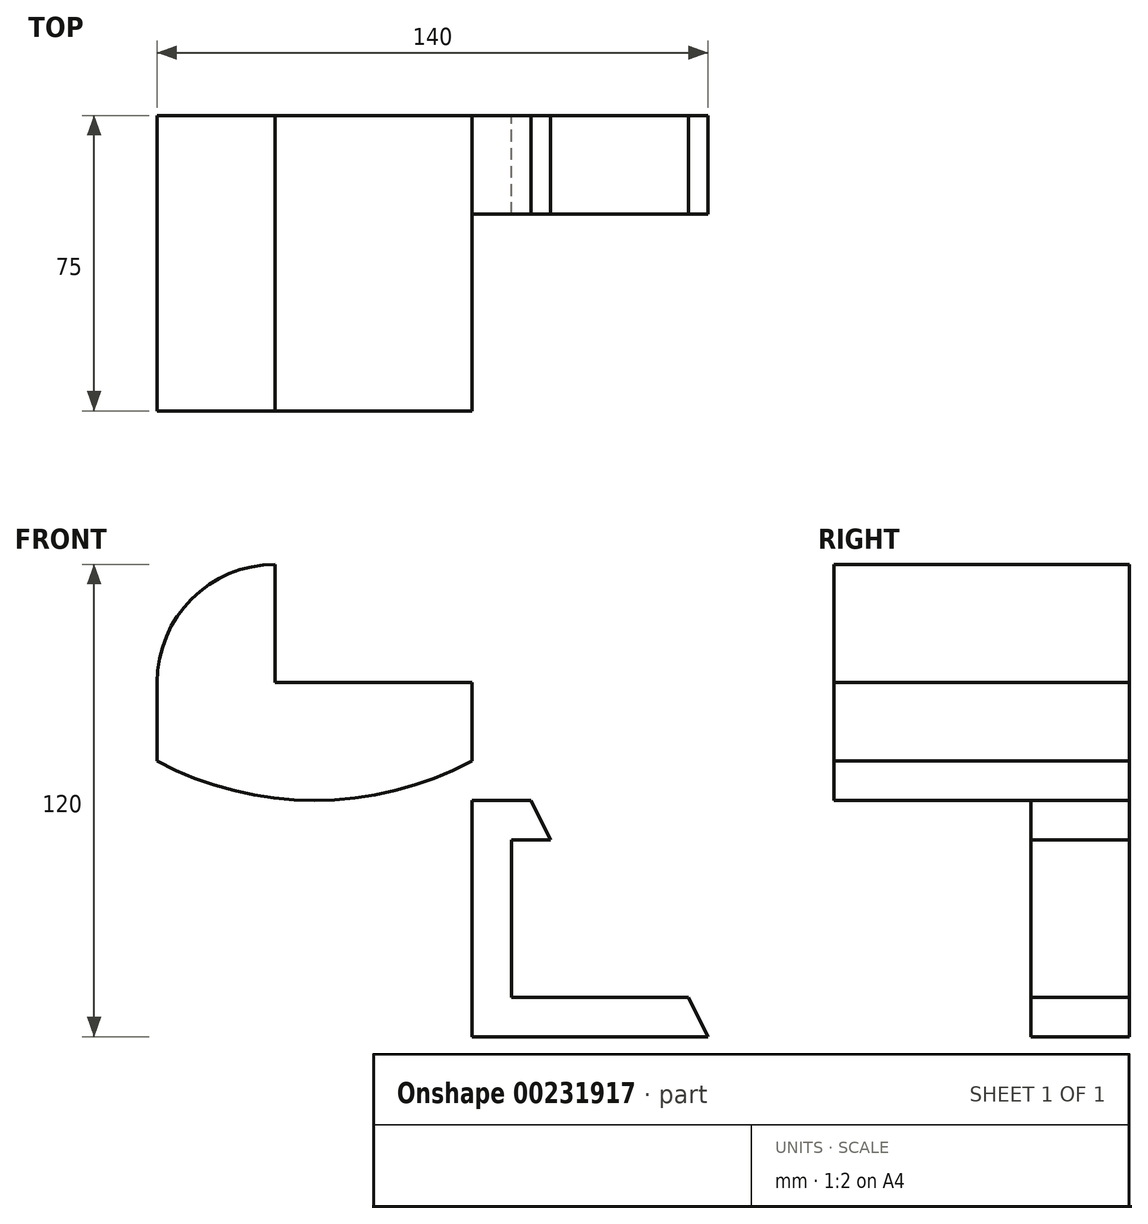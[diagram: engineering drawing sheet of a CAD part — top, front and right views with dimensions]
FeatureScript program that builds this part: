
annotation { "Feature Type Name" : "Feature", "Feature Type Description" : "" }
export const myFeature = defineFeature(function(context is Context, id is Id, definition is map)
    precondition{}
    {
        {
            var Q0;
            Q0=qCreatedBy(makeId("Front.planeOp"),FACE);
            var sketch = newSketch(context, id + "F0", { "sketchPlane" : qUnion([Q0])});
            skLineSegment(sketch, "E0", {"start": v(0, 0) * mm, "end": v(15, 0) * mm});
            skLineSegment(sketch, "E1", {"start": v(15, 0) * mm, "end": v(20, -10) * mm});
            skLineSegment(sketch, "E2", {"start": v(20, -10) * mm, "end": v(10, -10) * mm});
            skLineSegment(sketch, "E3", {"start": v(10, -10) * mm, "end": v(10, -50) * mm});
            skLineSegment(sketch, "E4", {"start": v(10, -50) * mm, "end": v(55, -50) * mm});
            skLineSegment(sketch, "E5", {"start": v(55, -50) * mm, "end": v(60, -60) * mm});
            skLineSegment(sketch, "E6", {"start": v(60, -60) * mm, "end": v(0, -60) * mm});
            skLineSegment(sketch, "E7", {"start": v(0, 0) * mm, "end": v(0, -60) * mm});
            skSolve(sketch);
        }
        {
            var Q0;
            Q0=qCreatedBy(makeId("Front.planeOp"),FACE);
            var sketch = newSketch(context, id + "F1", { "sketchPlane" : qUnion([Q0])});
            skLineSegment(sketch, "E8", {"start": v(-50, 30) * mm, "end": v(-50, 60) * mm});
            skArc(sketch, "E9", {"start": v(-50, 60) * mm, "mid": v(-71.21, 51.21) * mm, "end": v(-80, 30) * mm});
            skLineSegment(sketch, "E10", {"start": v(-80, 30) * mm, "end": v(-80, 10) * mm});
            skLineSegment(sketch, "E11", {"start": v(-50, 30) * mm, "end": v(0, 30) * mm});
            skLineSegment(sketch, "E12", {"start": v(0, 30) * mm, "end": v(0, 10) * mm});
            skArc(sketch, "E13", {"start": v(-80, 10) * mm, "mid": v(-40, 0) * mm, "end": v(0, 10) * mm});
            skSolve(sketch);
        }
        {
            var Q0;
            Q0=makeQuery(id+"F1.imprint","IMPRINT",FACE,{"disambiguationData":[TD([[makeQuery(id+"F1.imprint","IMPRINT",EDGE,{"derivedFrom":sQuery(id+"F1.wireOp",EDGE,"E8")}),1.0]])]});
            extrude(context, id + "F2", {"entities" : qUnion([Q0]), "depth" : 50 * mm});
        }
        {
            var Q0;
            Q0 = qSketchRegion(id + "F0", true);
            extrude(context, id + "F3", {"entities" : qUnion([Q0]), "depth" : 25 * mm});
        }
        {
            var Q0;
            Q0=makeQuery(id+"F2.opExtrude","CAP_FACE",FACE,{"disambiguationData":[OSD([sQuery(id+"F1.wireOp",EDGE,"E8"),sQuery(id+"F1.wireOp",EDGE,"E9"),sQuery(id+"F1.wireOp",EDGE,"E10"),sQuery(id+"F1.wireOp",EDGE,"E11"),sQuery(id+"F1.wireOp",EDGE,"E12"),sQuery(id+"F1.wireOp",EDGE,"E13")])],"isStart":false});
            extrude(context, id + "F4", {"entities" : qUnion([Q0]), "operationType" : NewBodyOperationType.ADD, "depth" : 25 * mm});
        }
    });
